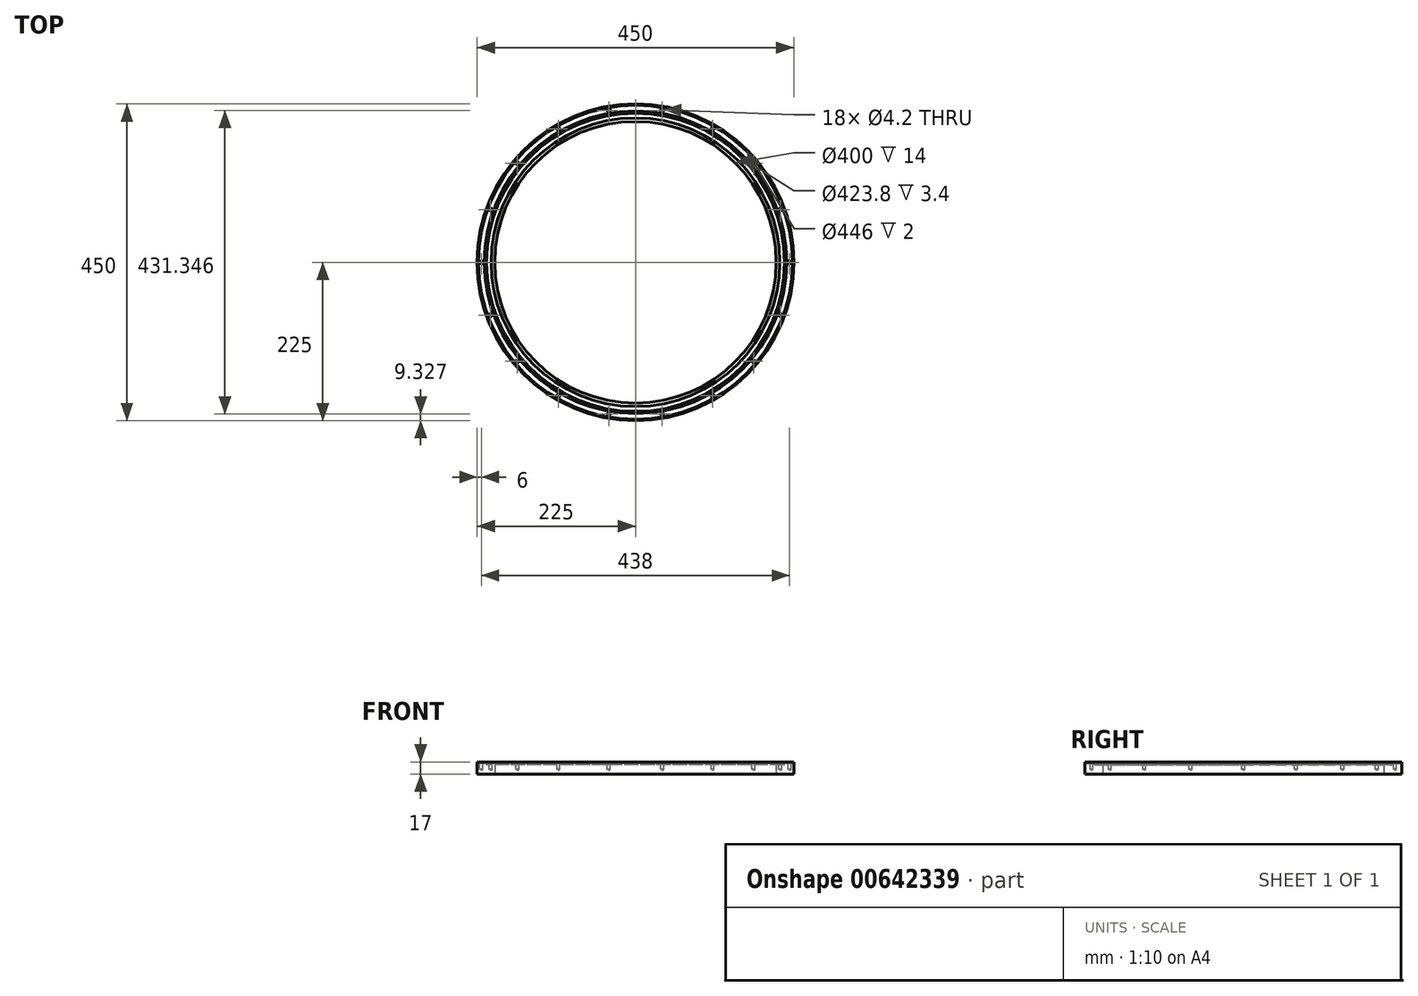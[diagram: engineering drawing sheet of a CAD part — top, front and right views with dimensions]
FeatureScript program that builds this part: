
annotation { "Feature Type Name" : "Feature", "Feature Type Description" : "" }
export const myFeature = defineFeature(function(context is Context, id is Id, definition is map)
    precondition{}
    {
        {
            var Q0;
            Q0=qCreatedBy(makeId("Top.planeOp"),FACE);
            var sketch = newSketch(context, id + "F0", { "sketchPlane" : qUnion([Q0])});
            skCircle(sketch, "E0", {"center": v(0, 0) * mm, "radius": 225 * mm});
            skCircle(sketch, "E1", {"center": v(0, 0) * mm, "radius": 200 * mm});
            skSolve(sketch);
        }
        {
            var Q0;
            Q0=makeQuery(id+"F0.imprint","IMPRINT",FACE,{"disambiguationData":[TD([[makeQuery(id+"F0.imprint","IMPRINT",EDGE,{"derivedFrom":sQuery(id+"F0.wireOp",EDGE,"E0")}),1.0]])]});
            extrude(context, id + "F1", {"entities" : qUnion([Q0]), "depth" : 17 * mm, "offsetDistance" : 25 * mm});
        }
        {
            var Q0;
            Q0=makeQuery(id+"F1.opExtrude","CAP_FACE",FACE,{"disambiguationData":[OSD([sQuery(id+"F0.wireOp",EDGE,"E0"),sQuery(id+"F0.wireOp",EDGE,"E1")])],"isStart":false});
            var sketch = newSketch(context, id + "F2", { "sketchPlane" : qUnion([Q0])});
            skCircle(sketch, "E2", {"center": v(0, 0) * mm, "radius": 205 * mm});
            skCircle(sketch, "E3", {"center": v(0, 0) * mm, "radius": 211.9 * mm});
            skSolve(sketch);
        }
        {
            var Q0;
            Q0=makeQuery(id+"F2.imprint","IMPRINT",FACE,{"disambiguationData":[TD([[makeQuery(id+"F2.imprint","IMPRINT",EDGE,{"derivedFrom":sQuery(id+"F2.wireOp",EDGE,"E2")}),-1.0]])]});
            extrude(context, id + "F3", {"entities" : qUnion([Q0]), "operationType" : NewBodyOperationType.REMOVE, "oppositeDirection" : true, "depth" : 4 * mm, "offsetDistance" : 25 * mm});
        }
        {
            var Q0;
            Q0=makeQuery(id+"F3.boolean.opBoolean","COPY",EDGE,{"derivedFrom":makeQuery(id+"F3.opExtrude","CAP_EDGE",EDGE,{"disambiguationData":[OSD([sQuery(id+"F2.wireOp",EDGE,"E3")])],"isStart":false})});
            var Q1;
            Q1=makeQuery(id+"F3.boolean.opBoolean","COPY",EDGE,{"derivedFrom":makeQuery(id+"F3.opExtrude","CAP_EDGE",EDGE,{"disambiguationData":[OSD([sQuery(id+"F2.wireOp",EDGE,"E2")])],"isStart":false})});
            fillet(context, id + "F4", {"entities" : qUnion([Q0, Q1]), "radius" : 0.6 * mm, "tangentPropagation" : true, "allowEdgeOverflow" : false});
        }
        {
            var Q0;
            {var subQ0=sQuery(id+"F0.wireOp",EDGE,"E0");Q0=makeQuery(id+"F3.boolean.opBoolean","SPLIT",FACE,{"disambiguationData":[TD([makeQuery(id+"F1.opExtrude","SWEPT_FACE",FACE,{"disambiguationData":[OSD([subQ0])]})])],"derivedFrom":makeQuery(id+"F1.opExtrude","CAP_FACE",FACE,{"disambiguationData":[OSD([subQ0,sQuery(id+"F0.wireOp",EDGE,"E1")])],"isStart":false})});}
            var sketch = newSketch(context, id + "F5", { "sketchPlane" : qUnion([Q0])});
            skCircle(sketch, "E4", {"center": v(0, 0) * mm, "radius": 223 * mm});
            skCircle(sketch, "E5", {"center": v(0, 0) * mm, "radius": 215 * mm});
            skSolve(sketch);
        }
        {
            var Q0;
            Q0=makeQuery(id+"F5.imprint","IMPRINT",FACE,{"disambiguationData":[TD([[makeQuery(id+"F5.imprint","IMPRINT",EDGE,{"derivedFrom":sQuery(id+"F5.wireOp",EDGE,"E4")}),1.0]])]});
            extrude(context, id + "F6", {"entities" : qUnion([Q0]), "operationType" : NewBodyOperationType.REMOVE, "oppositeDirection" : true, "depth" : 2 * mm, "offsetDistance" : 25 * mm});
        }
        {
            var Q0;
            Q0=makeQuery(id+"F1.opExtrude","CAP_EDGE",EDGE,{"disambiguationData":[OSD([sQuery(id+"F0.wireOp",EDGE,"E1")])],"isStart":false});
            fillet(context, id + "F7", {"entities" : qUnion([Q0]), "radius" : 3 * mm, "tangentPropagation" : true, "allowEdgeOverflow" : false});
        }
        {
            var Q0;
            Q0=makeQuery(id+"F6.boolean.opBoolean","COPY",FACE,{"derivedFrom":makeQuery(id+"F6.opExtrude","CAP_FACE",FACE,{"disambiguationData":[OSD([sQuery(id+"F5.wireOp",EDGE,"E4"),sQuery(id+"F5.wireOp",EDGE,"E5")])],"isStart":false})});
            var sketch = newSketch(context, id + "F8", { "sketchPlane" : qUnion([Q0])});
            skPoint(sketch, "E6", {"position": v(219, 0) * mm});
            skPoint(sketch, "E7.1.0", {"position": v(205.8, 74.9) * mm});
            skPoint(sketch, "E7.2.0", {"position": v(167.76, 140.77) * mm});
            skPoint(sketch, "E7.3.0", {"position": v(109.5, 189.66) * mm});
            skPoint(sketch, "E7.4.0", {"position": v(38.03, 215.67) * mm});
            skPoint(sketch, "E7.5.0", {"position": v(-38.03, 215.67) * mm});
            skPoint(sketch, "E7.6.0", {"position": v(-109.5, 189.66) * mm});
            skPoint(sketch, "E7.7.0", {"position": v(-167.76, 140.77) * mm});
            skPoint(sketch, "E7.8.0", {"position": v(-205.8, 74.9) * mm});
            skPoint(sketch, "E7.9.0", {"position": v(-219, 0) * mm});
            skPoint(sketch, "E7.10.0", {"position": v(-205.8, -74.9) * mm});
            skPoint(sketch, "E7.11.0", {"position": v(-167.76, -140.77) * mm});
            skPoint(sketch, "E7.12.0", {"position": v(-109.5, -189.66) * mm});
            skPoint(sketch, "E7.13.0", {"position": v(-38.03, -215.67) * mm});
            skPoint(sketch, "E7.14.0", {"position": v(38.03, -215.67) * mm});
            skPoint(sketch, "E7.15.0", {"position": v(109.5, -189.66) * mm});
            skPoint(sketch, "E7.16.0", {"position": v(167.76, -140.77) * mm});
            skPoint(sketch, "E7.17.0", {"position": v(205.8, -74.9) * mm});
            skPoint(sketch, "E7.center", {"position": v(0, 0) * mm});
            skLineSegment(sketch, "E8", {"start": v(0, 0) * mm, "end": v(205.8, 74.9) * mm, "construction": true});
            skSolve(sketch);
        }
        {
            var Q0;
            Q0=sQuery(id+"F8.wireOp",VERTEX,"E6");
            var Q1;
            Q1=sQuery(id+"F8.wireOp",VERTEX,"E7.1.0");
            var Q2;
            Q2=sQuery(id+"F8.wireOp",VERTEX,"E7.2.0");
            var Q3;
            Q3=sQuery(id+"F8.wireOp",VERTEX,"E7.3.0");
            var Q4;
            Q4=sQuery(id+"F8.wireOp",VERTEX,"E7.4.0");
            var Q5;
            Q5=sQuery(id+"F8.wireOp",VERTEX,"E7.5.0");
            var Q6;
            Q6=sQuery(id+"F8.wireOp",VERTEX,"E7.6.0");
            var Q7;
            Q7=sQuery(id+"F8.wireOp",VERTEX,"E7.7.0");
            var Q8;
            Q8=sQuery(id+"F8.wireOp",VERTEX,"E7.8.0");
            var Q9;
            Q9=sQuery(id+"F8.wireOp",VERTEX,"E7.9.0");
            var Q10;
            Q10=sQuery(id+"F8.wireOp",VERTEX,"E7.10.0");
            var Q11;
            Q11=sQuery(id+"F8.wireOp",VERTEX,"E7.11.0");
            var Q12;
            Q12=sQuery(id+"F8.wireOp",VERTEX,"E7.12.0");
            var Q13;
            Q13=sQuery(id+"F8.wireOp",VERTEX,"E7.13.0");
            var Q14;
            Q14=sQuery(id+"F8.wireOp",VERTEX,"E7.14.0");
            var Q15;
            Q15=sQuery(id+"F8.wireOp",VERTEX,"E7.15.0");
            var Q16;
            Q16=sQuery(id+"F8.wireOp",VERTEX,"E7.16.0");
            var Q17;
            Q17=sQuery(id+"F8.wireOp",VERTEX,"E7.17.0");
            var Q18;
            Q18=sQuery(id+"F8.wireOp",VERTEX,"E7.18.0");
            var Q19;
            Q19=sQuery(id+"F8.wireOp",VERTEX,"E7.19.0");
            var Q20;
            Q20=sQuery(id+"F8.wireOp",VERTEX,"E7.20.0");
            var Q21;
            Q21=sQuery(id+"F8.wireOp",VERTEX,"E7.21.0");
            var Q22;
            Q22=sQuery(id+"F8.wireOp",VERTEX,"E7.22.0");
            var Q23;
            Q23=sQuery(id+"F8.wireOp",VERTEX,"E7.23.0");
            var Q24;
            Q24=sQuery(id+"F8.wireOp",VERTEX,"60e13b0b-5bd3-436e-ac64-4843cf1f86f4.0.24.0");
            var Q25;
            Q25=sQuery(id+"F8.wireOp",VERTEX,"60e13b0b-5bd3-436e-ac64-4843cf1f86f4.0.25.0");
            var Q26;
            Q26=sQuery(id+"F8.wireOp",VERTEX,"60e13b0b-5bd3-436e-ac64-4843cf1f86f4.0.26.0");
            var Q27;
            Q27=sQuery(id+"F8.wireOp",VERTEX,"60e13b0b-5bd3-436e-ac64-4843cf1f86f4.0.27.0");
            var Q28;
            Q28=sQuery(id+"F8.wireOp",VERTEX,"60e13b0b-5bd3-436e-ac64-4843cf1f86f4.0.28.0");
            var Q29;
            Q29=sQuery(id+"F8.wireOp",VERTEX,"60e13b0b-5bd3-436e-ac64-4843cf1f86f4.0.29.0");
            var Q30;
            Q30=sQuery(id+"F8.wireOp",VERTEX,"60e13b0b-5bd3-436e-ac64-4843cf1f86f4.0.30.0");
            var Q31;
            Q31=sQuery(id+"F8.wireOp",VERTEX,"60e13b0b-5bd3-436e-ac64-4843cf1f86f4.0.31.0");
            var Q32;
            Q32=sQuery(id+"F8.wireOp",VERTEX,"60e13b0b-5bd3-436e-ac64-4843cf1f86f4.0.32.0");
            var Q33;
            Q33=sQuery(id+"F8.wireOp",VERTEX,"60e13b0b-5bd3-436e-ac64-4843cf1f86f4.0.33.0");
            var Q34;
            Q34=sQuery(id+"F8.wireOp",VERTEX,"60e13b0b-5bd3-436e-ac64-4843cf1f86f4.0.34.0");
            var Q35;
            Q35=sQuery(id+"F8.wireOp",VERTEX,"60e13b0b-5bd3-436e-ac64-4843cf1f86f4.0.35.0");
            var Q36;
            Q36=makeQuery(id+"F1.opExtrude","SWEPT_BODY",BODY,{"disambiguationData":[OSD([sQuery(id+"F0.wireOp",EDGE,"E0"),sQuery(id+"F0.wireOp",EDGE,"E1")])]});
            hole(context, id + "F9", {"style" : HoleStyle.SIMPLE, "endStyle" : HoleEndStyle.BLIND, "standardTappedOrClearance" : lookupTablePath({ "standard" : "ISO", "engagement" : "75%", "pitch" : "0.8 mm", "size" : "M5", "type" : "Tapped" }), "standardBlindInLast" : lookupTablePath({ "standard" : "ISO", "engagement" : "75%", "pitch" : "0.8 mm", "size" : "M5", "type" : "Tapped" }), "holeDiameter" : 4.2 * mm, "majorDiameter" : 5 * mm, "showTappedDepth" : true, "holeDepth" : 8.6 * mm, "isTappedThrough" : true, "tappedDepth" : 7 * mm, "tapClearance" : 2, "locations" : qUnion([Q0, Q1, Q2, Q3, Q4, Q5, Q6, Q7, Q8, Q9, Q10, Q11, Q12, Q13, Q14, Q15, Q16, Q17, Q18, Q19, Q20, Q21, Q22, Q23, Q24, Q25, Q26, Q27, Q28, Q29, Q30, Q31, Q32, Q33, Q34, Q35]), "scope" : qUnion([Q36])});
        }
    });
